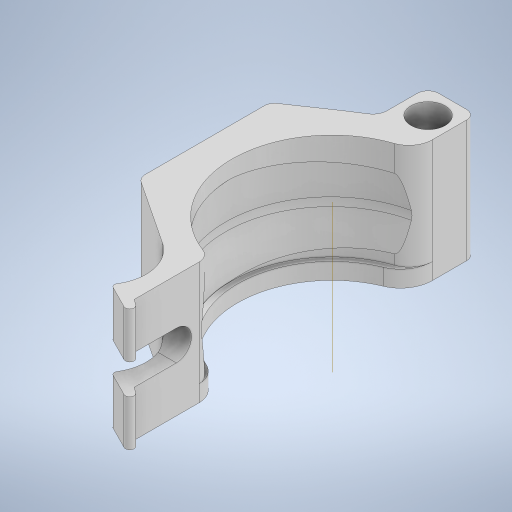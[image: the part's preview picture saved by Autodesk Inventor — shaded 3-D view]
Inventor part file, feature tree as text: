
AUTODESK INVENTOR PART (.ipt)
format: ipt  version: 2023 (Build 270158000, 158)  size: 5,153,280 bytes
history: native  units: in
note: dims shown in document units (in); Inventor stores cm internally (conversion verified against a paired STEP export)
features: sketch x4, extrude x3, other x3, plane x1, revolve x1
ambient origin geometry x8: Origin, YZ Plane, XZ Plane, XY Plane, X Axis, Y Axis, Z Axis, Center Point
bodies: Solid1 (feature_tree)
feature tree (12):
  extrude  "Extrusion1"  Depth=0.2461in
  extrude  "Extrusion2"  Depth=0.0394in
  extrude  "Extrusion3"  Depth=0.2165in
  other  "Work Axis1"
  plane  "Work Plane1"
  revolve  "Revolution1"  [1 undecoded]
  sketch  "Sketch1"  dims[d10=0.0787in d24=0.2461in]
  other  "Image1"
  other  "Image2"
  sketch  "Sketch2"  dims[d141=0.876in d142=0.0in d143=0.0394in]
  sketch  "Sketch3"  dims[d144=0.1181in d145=0.0in d146=0.2165in]
  sketch  "Sketch4"  dims[d147=0.876in d148=0.438in d149=0.7874in d150=0.3937in d151=0.0in d152=-0.1259in d153=0.1181in d154=0.2362in d155=0.0394in d156=90.0deg d170=0.7185in]
note: 1 required parameter value undecoded (feature->parameter linkage not recoverable at this tier; creation-order binding heuristic only, values carry confidence <= 0.55)
